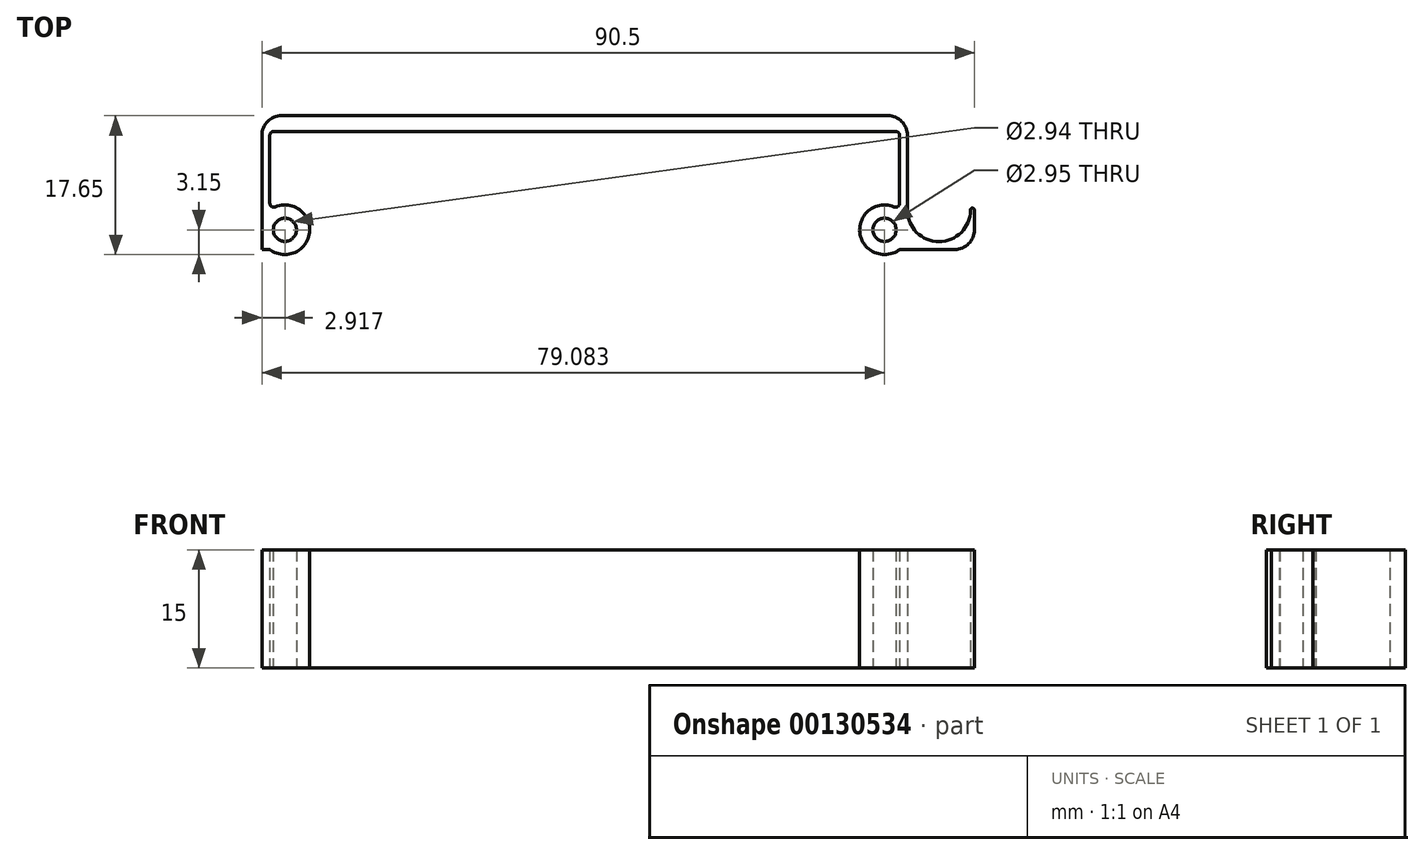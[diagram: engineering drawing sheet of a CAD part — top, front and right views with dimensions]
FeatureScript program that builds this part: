
annotation { "Feature Type Name" : "Feature", "Feature Type Description" : "" }
export const myFeature = defineFeature(function(context is Context, id is Id, definition is map)
    precondition{}
    {
        {
            var Q0;
            Q0=qCreatedBy(makeId("Top.planeOp"),FACE);
            var sketch = newSketch(context, id + "F0", { "sketchPlane" : qUnion([Q0])});
            skLineSegment(sketch, "E0", {"start": v(0, 0) * mm, "end": v(-39.5, 0) * mm});
            skLineSegment(sketch, "E1", {"start": v(-40, -0.5) * mm, "end": v(-40, -9.14) * mm});
            skLineSegment(sketch, "E2", {"start": v(-41, -15) * mm, "end": v(-40.16, -15) * mm});
            skArc(sketch, "E3", {"start": v(-39.88, -15.09) * mm, "mid": v(-34.95, -12.83) * mm, "end": v(-39.3, -9.6) * mm});
            skPoint(sketch, "E3.third.point", {"position": v(-34.93, -12.42) * mm});
            skArc(sketch, "E4.MirrorCS", {"start": v(39.88, -15.09) * mm, "mid": v(34.95, -12.83) * mm, "end": v(39.3, -9.6) * mm});
            skLineSegment(sketch, "E5.MirrorCS", {"start": v(45, -15) * mm, "end": v(40.16, -15) * mm});
            skPoint(sketch, "E6.MirrorP", {"position": v(34.93, -12.42) * mm});
            skLineSegment(sketch, "E7.MirrorCS", {"start": v(0, 0) * mm, "end": v(39.5, 0) * mm});
            skLineSegment(sketch, "E8.MirrorCS", {"start": v(40, -0.5) * mm, "end": v(40, -9.14) * mm});
            skLineSegment(sketch, "E9", {"start": v(45, -15) * mm, "end": v(47, -15) * mm});
            skPoint(sketch, "E10.visualSharp", {"position": v(40, -10) * mm});
            skArc(sketch, "E10.filletArc", {"start": v(39.3, -9.6) * mm, "mid": v(39.78, -9.55) * mm, "end": v(40, -9.14) * mm});
            skPoint(sketch, "E11.visualSharp", {"position": v(40, -15) * mm});
            skArc(sketch, "E11.filletArc", {"start": v(40.16, -15) * mm, "mid": v(40.01, -15.02) * mm, "end": v(39.88, -15.09) * mm});
            skPoint(sketch, "E12.visualSharp", {"position": v(40, 0) * mm});
            skArc(sketch, "E12.filletArc", {"start": v(40, -0.5) * mm, "mid": v(39.85, -0.15) * mm, "end": v(39.5, 0) * mm});
            skPoint(sketch, "E13.visualSharp", {"position": v(-40, -10) * mm});
            skArc(sketch, "E13.filletArc", {"start": v(-40, -9.14) * mm, "mid": v(-39.78, -9.55) * mm, "end": v(-39.3, -9.6) * mm});
            skPoint(sketch, "E14.visualSharp", {"position": v(-40, 0) * mm});
            skArc(sketch, "E14.filletArc", {"start": v(-39.5, 0) * mm, "mid": v(-39.85, -0.15) * mm, "end": v(-40, -0.5) * mm});
            skPoint(sketch, "E15.visualSharp", {"position": v(-40, -15) * mm});
            skArc(sketch, "E15.filletArc", {"start": v(-39.88, -15.09) * mm, "mid": v(-40.01, -15.02) * mm, "end": v(-40.16, -15) * mm});
            skLineSegment(sketch, "E16", {"start": v(0, 0) * mm, "end": v(0, 2) * mm});
            skLineSegment(sketch, "E17", {"start": v(-38.5, 2) * mm, "end": v(38.5, 2) * mm});
            skLineSegment(sketch, "E18", {"start": v(41, -2.57) * mm, "end": v(41, -0.5) * mm});
            skLineSegment(sketch, "E19", {"start": v(-41, -0.5) * mm, "end": v(-41, -15) * mm});
            skArc(sketch, "E20", {"start": v(41, -10) * mm, "mid": v(45, -14) * mm, "end": v(49, -10) * mm});
            skArc(sketch, "E21", {"start": v(49.5, -10) * mm, "mid": v(49.25, -9.75) * mm, "end": v(49, -10) * mm});
            skLineSegment(sketch, "E22", {"start": v(49.5, -10) * mm, "end": v(49.5, -12.5) * mm});
            skPoint(sketch, "E23.visualSharp", {"position": v(41, 2) * mm});
            skArc(sketch, "E23.filletArc", {"start": v(41, -0.5) * mm, "mid": v(40.27, 1.27) * mm, "end": v(38.5, 2) * mm});
            skPoint(sketch, "E24.visualSharp", {"position": v(49.5, -15) * mm});
            skArc(sketch, "E24.filletArc", {"start": v(47, -15) * mm, "mid": v(48.77, -14.27) * mm, "end": v(49.5, -12.5) * mm});
            skPoint(sketch, "E25.visualSharp", {"position": v(-41, 2) * mm});
            skArc(sketch, "E25.filletArc", {"start": v(-38.5, 2) * mm, "mid": v(-40.27, 1.27) * mm, "end": v(-41, -0.5) * mm});
            skLineSegment(sketch, "E26", {"start": v(41, -10) * mm, "end": v(41, -2.57) * mm});
            skCircle(sketch, "E27", {"center": v(-38.08, -12.5) * mm, "radius": 1.47 * mm});
            skCircle(sketch, "E28", {"center": v(38.08, -12.5) * mm, "radius": 1.48 * mm});
            skSolve(sketch);
        }
        {
            var Q0;
            Q0 = qSketchRegion(id + "F0", true);
            extrude(context, id + "F1", {"entities" : qUnion([Q0]), "depth" : 15 * mm});
        }
    });
